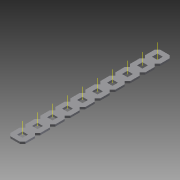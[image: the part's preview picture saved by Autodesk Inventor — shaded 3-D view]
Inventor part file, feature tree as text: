
AUTODESK INVENTOR PART (.ipt)
format: ipt  version: 2015 (Build 190159000, 159)  size: 1,137,664 bytes
history: native  units: in
note: dims shown in document units (in); Inventor stores cm internally (conversion verified against a paired STEP export)
features: other x19, extrude x2, pattern_linear x1, imported_body x1
ambient origin geometry x8: Origin, YZ Plane, XZ Plane, XY Plane, X Axis, Y Axis, Z Axis, Center Point
bodies: Body1 (feature_tree)
feature tree (23):
  other  "Diamond-Pattern"
  other  "Plate"
  extrude  "length cut"  TaperAngle=0.0deg  [1 undecoded]
  extrude  "width cut"  TaperAngle=0.0deg  [1 undecoded]
  other  "constraint axis"
  pattern_linear  "constraint axes"  Spacing1=0.5in  [1 undecoded]
  other  "front plane"
  other  "right plane"
  imported_body  "Base1"
  other  "length profile"
  other  "width profile"
  other  "Work Point1"
  other  "back plane"
  other  "left plane"
  other  "Work Axis170"
  other  "Work Axis171"
  other  "Work Axis172"
  other  "Work Axis173"
  other  "Work Axis174"
  other  "Work Axis175"
  other  "Work Axis176"
  other  "Work Axis177"
  other  "Work Axis178"
note: 3 required parameter values undecoded (feature->parameter linkage not recoverable at this tier; creation-order binding heuristic only, values carry confidence <= 0.55)
